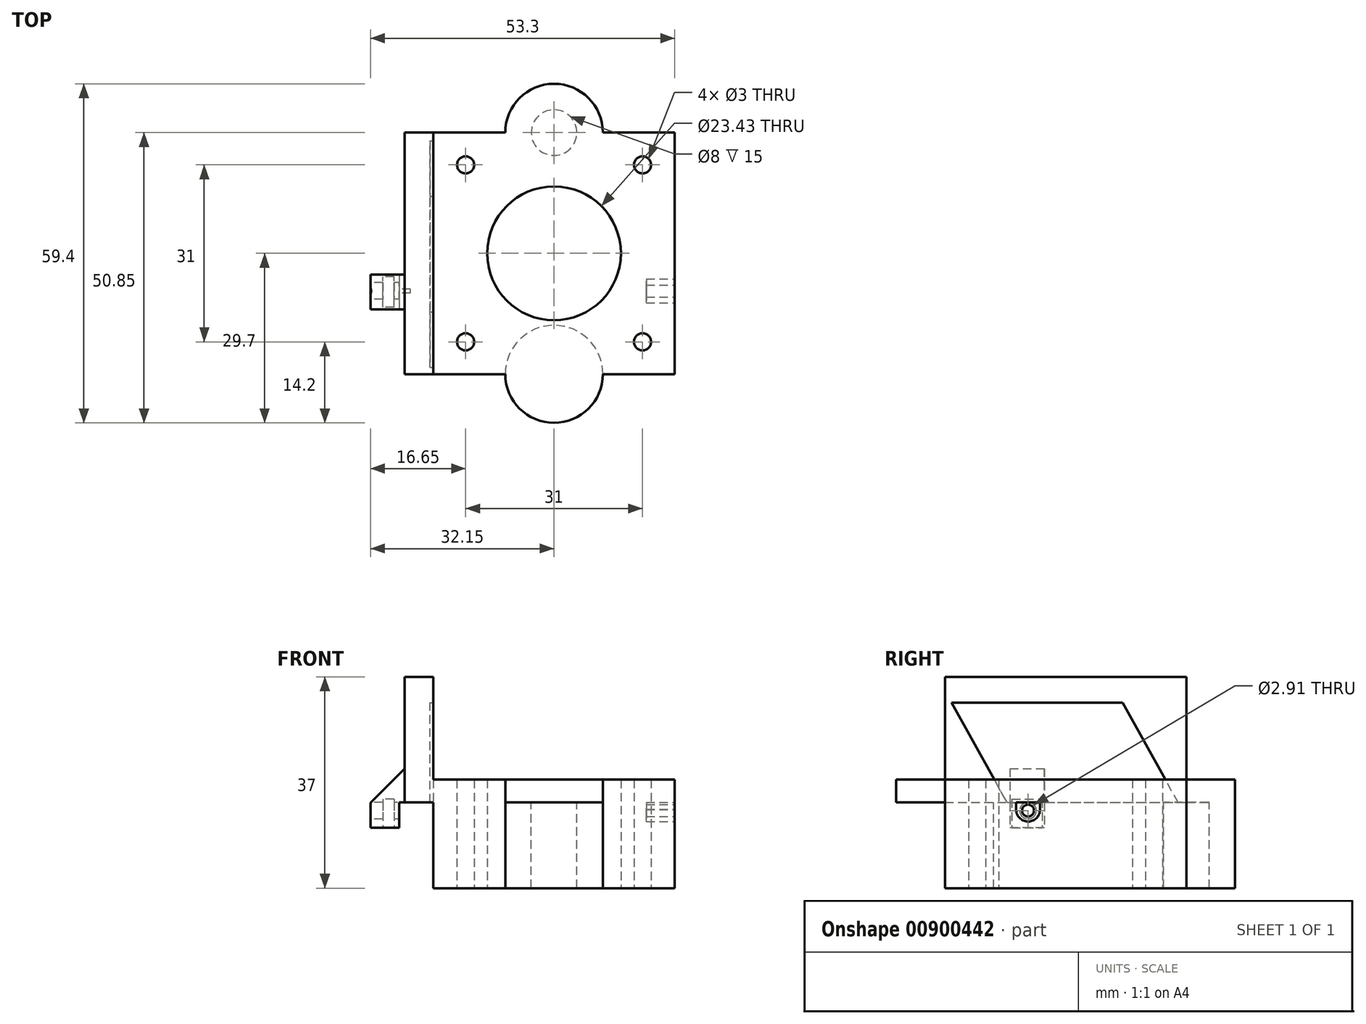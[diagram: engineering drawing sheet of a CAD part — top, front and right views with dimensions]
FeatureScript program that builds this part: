
annotation { "Feature Type Name" : "Feature", "Feature Type Description" : "" }
export const myFeature = defineFeature(function(context is Context, id is Id, definition is map)
    precondition{}
    {
        {
            var Q0;
            Q0=qCreatedBy(makeId("Top.planeOp"),FACE);
            var sketch = newSketch(context, id + "F0", { "sketchPlane" : qUnion([Q0])});
            skLineSegment(sketch, "E0.bottom", {"start": v(21.15, 21.15) * mm, "end": v(8.55, 21.15) * mm});
            skLineSegment(sketch, "E0.top", {"start": v(21.15, -21.15) * mm, "end": v(8.55, -21.15) * mm});
            skLineSegment(sketch, "E0.left", {"start": v(21.15, 21.15) * mm, "end": v(21.15, -21.15) * mm});
            skLineSegment(sketch, "E0.right", {"start": v(-21.15, 21.15) * mm, "end": v(-21.15, -21.15) * mm});
            skPoint(sketch, "E0.middle", {"position": v(0, 0) * mm});
            skCircle(sketch, "E1", {"center": v(-15.5, 15.5) * mm, "radius": 1.5 * mm});
            skCircle(sketch, "E2", {"center": v(15.5, 15.5) * mm, "radius": 1.5 * mm});
            skCircle(sketch, "E3", {"center": v(-15.5, -15.5) * mm, "radius": 1.5 * mm});
            skCircle(sketch, "E4", {"center": v(15.5, -15.5) * mm, "radius": 1.5 * mm});
            skCircle(sketch, "E5", {"center": v(0, 0) * mm, "radius": 11.71 * mm});
            skArc(sketch, "E6", {"start": v(0, 29.7) * mm, "mid": v(6.04, 27.2) * mm, "end": v(8.55, 21.15) * mm});
            skPoint(sketch, "E6.startSnap0", {"position": v(0, 21.15) * mm});
            skArc(sketch, "E7", {"start": v(0, 29.7) * mm, "mid": v(-6.04, 27.2) * mm, "end": v(-8.55, 21.15) * mm});
            skArc(sketch, "E8", {"start": v(-8.55, -21.15) * mm, "mid": v(0, -29.7) * mm, "end": v(8.55, -21.15) * mm});
            skLineSegment(sketch, "E9.trimOffspring", {"start": v(-8.55, -21.15) * mm, "end": v(-21.15, -21.15) * mm});
            skLineSegment(sketch, "E10.trimOffspring", {"start": v(-8.55, 21.15) * mm, "end": v(-21.15, 21.15) * mm});
            skSolve(sketch);
        }
        {
            var Q0;
            Q0=makeQuery(id+"F0.imprint","IMPRINT",FACE,{"disambiguationData":[TD([[makeQuery(id+"F0.imprint","IMPRINT",EDGE,{"derivedFrom":sQuery(id+"F0.wireOp",EDGE,"E0.bottom")}),1.0]])]});
            extrude(context, id + "F1", {"entities" : qUnion([Q0]), "depth" : 4 * mm, "offsetDistance" : 25 * mm});
        }
        {
            var Q0;
            Q0=makeQuery(id+"F1.opExtrude","CAP_FACE",FACE,{"disambiguationData":[OSD([sQuery(id+"F0.wireOp",EDGE,"E0.bottom"),sQuery(id+"F0.wireOp",EDGE,"E0.top"),sQuery(id+"F0.wireOp",EDGE,"E0.left"),sQuery(id+"F0.wireOp",EDGE,"E0.right"),sQuery(id+"F0.wireOp",EDGE,"E1"),sQuery(id+"F0.wireOp",EDGE,"E2"),sQuery(id+"F0.wireOp",EDGE,"E3"),sQuery(id+"F0.wireOp",EDGE,"E4"),sQuery(id+"F0.wireOp",EDGE,"E5"),sQuery(id+"F0.wireOp",EDGE,"E6"),sQuery(id+"F0.wireOp",EDGE,"E7"),sQuery(id+"F0.wireOp",EDGE,"E8"),sQuery(id+"F0.wireOp",EDGE,"E9.trimOffspring"),sQuery(id+"F0.wireOp",EDGE,"E10.trimOffspring")])],"isStart":true});
            var sketch = newSketch(context, id + "F2", { "sketchPlane" : qUnion([Q0])});
            skCircle(sketch, "E11", {"center": v(0, 21.15) * mm, "radius": 8.55 * mm});
            skCircle(sketch, "E12", {"center": v(0, 21.15) * mm, "radius": 4 * mm});
            skCircle(sketch, "E13", {"center": v(0, -21.15) * mm, "radius": 8.55 * mm});
            skCircle(sketch, "E14", {"center": v(0, -21.15) * mm, "radius": 4 * mm});
            skSolve(sketch);
        }
        {
            var Q0;
            Q0=makeQuery(id+"F2.imprint","IMPRINT",FACE,{"disambiguationData":[TD([[makeQuery(id+"F2.imprint","IMPRINT",EDGE,{"derivedFrom":sQuery(id+"F2.wireOp",EDGE,"E14")}),-1.0]])]});
            var Q1;
            {var subQ0=sQuery(id+"F2.wireOp",EDGE,"E11");Q1=makeQuery(id+"F2.imprint","IMPRINT",FACE,{"disambiguationData":[TD([[makeQuery(id+"F2.imprint","IMPRINT",EDGE,{"disambiguationData":[OD(0.0)],"derivedFrom":subQ0}),-1.0]])]});}
            extrude(context, id + "F3", {"entities" : qUnion([Q0, Q1]), "operationType" : NewBodyOperationType.ADD, "depth" : 15 * mm, "offsetDistance" : 25 * mm});
        }
        {
            var Q0;
            Q0=makeQuery(id+"F1.opExtrude","SWEPT_FACE",FACE,{"disambiguationData":[OSD([sQuery(id+"F0.wireOp",EDGE,"E0.right")])]});
            cPlane(context, id + "F4", {"entities" : qUnion([Q0]), "cplaneType" : CPlaneType.OFFSET, "offset" : 0 * mm, "width" : 150 * mm, "height" : 150 * mm});
        }
        {
            var Q0;
            Q0=qCreatedBy(id+"F4.planeOp",FACE);
            var sketch = newSketch(context, id + "F5", { "sketchPlane" : qUnion([Q0])});
            skLineSegment(sketch, "E15.bottom", {"start": v(-20, -0.53) * mm, "end": v(20, -0.53) * mm});
            skLineSegment(sketch, "E15.top", {"start": v(-20, 17.47) * mm, "end": v(20, 17.47) * mm});
            skLineSegment(sketch, "E15.left", {"start": v(-20, -0.53) * mm, "end": v(-20, 17.47) * mm});
            skLineSegment(sketch, "E15.right", {"start": v(20, -0.53) * mm, "end": v(20, 17.47) * mm});
            skPoint(sketch, "E15.middle", {"position": v(0, 8.47) * mm});
            skLineSegment(sketch, "E16", {"start": v(20, 17.47) * mm, "end": v(10, -0.53) * mm});
            skLineSegment(sketch, "E17", {"start": v(-20, -0.53) * mm, "end": v(-10, 17.47) * mm});
            skSolve(sketch);
        }
        {
            var Q0;
            {var subQ2=sQuery(id+"F5.wireOp",EDGE,"E16");Q0=makeQuery(id+"F5.imprint","IMPRINT",FACE,{"disambiguationData":[TD([[makeQuery(id+"F5.imprint","IMPRINT",EDGE,{"derivedFrom":subQ2}),-1.0]])]});}
            extrude(context, id + "F6", {"entities" : qUnion([Q0]), "depth" : 0.6 * mm, "offsetDistance" : 25 * mm});
        }
        {
            var Q0;
            Q0=makeQuery(id+"F1.opExtrude","SWEPT_FACE",FACE,{"disambiguationData":[OSD([sQuery(id+"F0.wireOp",EDGE,"E0.right")])]});
            var sketch = newSketch(context, id + "F7", { "sketchPlane" : qUnion([Q0])});
            skLineSegment(sketch, "E18.bottom", {"start": v(21.15, 0) * mm, "end": v(-21.15, 0) * mm});
            skLineSegment(sketch, "E18.top", {"start": v(21.15, 22) * mm, "end": v(-21.15, 22) * mm});
            skLineSegment(sketch, "E18.left", {"start": v(21.15, 0) * mm, "end": v(21.15, 22) * mm});
            skLineSegment(sketch, "E18.right", {"start": v(-21.15, 0) * mm, "end": v(-21.15, 22) * mm});
            skSolve(sketch);
        }
        {
            var Q0;
            Q0 = qSketchRegion(id + "F7", true);
            extrude(context, id + "F8", {"entities" : qUnion([Q0]), "depth" : 5 * mm, "offsetDistance" : 25 * mm});
        }
        {
            var Q0;
            Q0=makeQuery(id+"F8.opExtrude","SWEPT_BODY",BODY,{"disambiguationData":[OSD([sQuery(id+"F7.wireOp",EDGE,"E18.bottom"),sQuery(id+"F7.wireOp",EDGE,"E18.top"),sQuery(id+"F7.wireOp",EDGE,"E18.left"),sQuery(id+"F7.wireOp",EDGE,"E18.right")])]});
            var Q1;
            Q1=makeQuery(id+"F1.opExtrude","SWEPT_BODY",BODY,{"disambiguationData":[OSD([sQuery(id+"F0.wireOp",EDGE,"E0.bottom"),sQuery(id+"F0.wireOp",EDGE,"E0.top"),sQuery(id+"F0.wireOp",EDGE,"E0.left"),sQuery(id+"F0.wireOp",EDGE,"E0.right"),sQuery(id+"F0.wireOp",EDGE,"E1"),sQuery(id+"F0.wireOp",EDGE,"E2"),sQuery(id+"F0.wireOp",EDGE,"E3"),sQuery(id+"F0.wireOp",EDGE,"E4"),sQuery(id+"F0.wireOp",EDGE,"E5"),sQuery(id+"F0.wireOp",EDGE,"E6"),sQuery(id+"F0.wireOp",EDGE,"E7"),sQuery(id+"F0.wireOp",EDGE,"E8"),sQuery(id+"F0.wireOp",EDGE,"E9.trimOffspring"),sQuery(id+"F0.wireOp",EDGE,"E10.trimOffspring")])]});
            booleanBodies(context, id + "F9", {"operationType" : BooleanOperationType.UNION, "tools" : qUnion([Q0, Q1])});
        }
        {
            var Q0;
            Q0=makeQuery(id+"F6.opExtrude","SWEPT_BODY",BODY,{"disambiguationData":[OSD([sQuery(id+"F5.wireOp",EDGE,"E15.bottom"),sQuery(id+"F5.wireOp",EDGE,"E15.top"),sQuery(id+"F5.wireOp",EDGE,"E16"),sQuery(id+"F5.wireOp",EDGE,"E17")])]});
            var Q1;
            Q1=makeQuery(id+"F8.opExtrude","SWEPT_BODY",BODY,{"disambiguationData":[OSD([sQuery(id+"F7.wireOp",EDGE,"E18.bottom"),sQuery(id+"F7.wireOp",EDGE,"E18.top"),sQuery(id+"F7.wireOp",EDGE,"E18.left"),sQuery(id+"F7.wireOp",EDGE,"E18.right")])]});
            booleanBodies(context, id + "F10", {"operationType" : BooleanOperationType.SUBTRACTION, "tools" : qUnion([Q0]), "targets" : qUnion([Q1])});
        }
        {
            var Q0;
            Q0=makeQuery(id+"F1.opExtrude","SWEPT_FACE",FACE,{"disambiguationData":[OSD([sQuery(id+"F0.wireOp",EDGE,"E0.left")])]});
            var sketch = newSketch(context, id + "F11", { "sketchPlane" : qUnion([Q0])});
            skLineSegment(sketch, "E19.bottom", {"start": v(-4.5, 0) * mm, "end": v(-8.7, 0) * mm});
            skLineSegment(sketch, "E19.left", {"start": v(-4.5, 0) * mm, "end": v(-4.5, -1.2) * mm});
            skLineSegment(sketch, "E19.right", {"start": v(-8.7, 0) * mm, "end": v(-8.7, -1.26) * mm});
            skArc(sketch, "E20", {"start": v(-4.5, -1.2) * mm, "mid": v(-6.57, -3.33) * mm, "end": v(-8.7, -1.26) * mm});
            skCircle(sketch, "E21", {"center": v(-6.6, -1.42) * mm, "radius": 1.04 * mm});
            skSolve(sketch);
        }
        {
            var Q0;
            Q0=makeQuery(id+"F11.imprint","IMPRINT",FACE,{"disambiguationData":[TD([[makeQuery(id+"F11.imprint","IMPRINT",EDGE,{"derivedFrom":sQuery(id+"F11.wireOp",EDGE,"E19.bottom")}),1.0]])]});
            extrude(context, id + "F12", {"entities" : qUnion([Q0]), "oppositeDirection" : true, "depth" : 5 * mm, "offsetDistance" : 25 * mm});
        }
        {
            var Q0;
            Q0=makeQuery(id+"F12.opExtrude","CAP_FACE",FACE,{"disambiguationData":[OSD([sQuery(id+"F11.wireOp",EDGE,"E19.bottom"),sQuery(id+"F11.wireOp",EDGE,"E19.left"),sQuery(id+"F11.wireOp",EDGE,"E19.right"),sQuery(id+"F11.wireOp",EDGE,"E20"),sQuery(id+"F11.wireOp",EDGE,"E21")])],"isStart":false});
            cPlane(context, id + "F13", {"entities" : qUnion([Q0]), "cplaneType" : CPlaneType.OFFSET, "offset" : 33.4 * mm, "width" : 150 * mm, "height" : 150 * mm});
        }
        {
            var Q0;
            Q0=qCreatedBy(id+"F13.planeOp",FACE);
            var sketch = newSketch(context, id + "F14", { "sketchPlane" : qUnion([Q0])});
            skLineSegment(sketch, "E22.0.0", {"start": v(8.7, 0) * mm, "end": v(4.5, 0) * mm});
            skLineSegment(sketch, "E22.0.1", {"start": v(4.5, 0) * mm, "end": v(4.5, -1.2) * mm});
            skArc(sketch, "E22.0.2", {"start": v(4.5, -1.2) * mm, "mid": v(6.57, -3.33) * mm, "end": v(8.7, -1.26) * mm});
            skLineSegment(sketch, "E22.0.3", {"start": v(8.7, -1.26) * mm, "end": v(8.7, 0) * mm});
            skCircle(sketch, "E23.0", {"center": v(6.6, -1.42) * mm, "radius": 1.04 * mm});
            skSolve(sketch);
        }
        {
            var Q0;
            Q0 = qSketchRegion(id + "F14", true);
            extrude(context, id + "F15", {"entities" : qUnion([Q0]), "operationType" : NewBodyOperationType.ADD, "oppositeDirection" : true, "depth" : 5 * mm, "offsetDistance" : 25 * mm});
        }
        {
            var Q0;
            Q0=makeQuery(id+"F8.opExtrude","CAP_FACE",FACE,{"disambiguationData":[OSD([sQuery(id+"F7.wireOp",EDGE,"E18.bottom"),sQuery(id+"F7.wireOp",EDGE,"E18.top"),sQuery(id+"F7.wireOp",EDGE,"E18.left"),sQuery(id+"F7.wireOp",EDGE,"E18.right")])],"isStart":false});
            var sketch = newSketch(context, id + "F16", { "sketchPlane" : qUnion([Q0])});
            skCircle(sketch, "E24.0", {"center": v(6.6, -1.42) * mm, "radius": 1.04 * mm});
            skArc(sketch, "E25.0", {"start": v(4.5, -1.2) * mm, "mid": v(6.57, -3.33) * mm, "end": v(8.7, -1.26) * mm});
            skLineSegment(sketch, "E26.0.1", {"start": v(8.7, -1.26) * mm, "end": v(8.7, 0) * mm});
            skLineSegment(sketch, "E26.0.2", {"start": v(8.7, 0) * mm, "end": v(4.5, 0) * mm});
            skLineSegment(sketch, "E26.0.3", {"start": v(4.5, 0) * mm, "end": v(4.5, -1.2) * mm});
            skLineSegment(sketch, "E27.bottom", {"start": v(9.8, 5.94) * mm, "end": v(3.74, 5.94) * mm});
            skLineSegment(sketch, "E27.top", {"start": v(9.8, -4.4) * mm, "end": v(3.74, -4.4) * mm});
            skLineSegment(sketch, "E27.left", {"start": v(9.8, 5.94) * mm, "end": v(9.8, -4.4) * mm});
            skLineSegment(sketch, "E27.right", {"start": v(3.74, 5.94) * mm, "end": v(3.74, -4.4) * mm});
            skSolve(sketch);
        }
        {
            var Q0;
            Q0 = qSketchRegion(id + "F16", true);
            var Q1;
            Q1=makeQuery(id+"F16.imprint","IMPRINT",FACE,{"disambiguationData":[TD([[makeQuery(id+"F16.imprint","IMPRINT",EDGE,{"derivedFrom":sQuery(id+"F16.wireOp",EDGE,"E25.0")}),-1.0]])]});
            var Q2;
            Q2=makeQuery(id+"F16.imprint","IMPRINT",FACE,{"disambiguationData":[TD([[makeQuery(id+"F16.imprint","IMPRINT",EDGE,{"derivedFrom":sQuery(id+"F16.wireOp",EDGE,"E24.0")}),-1.0]])]});
            extrude(context, id + "F17", {"entities" : qUnion([Q0, Q1, Q2]), "operationType" : NewBodyOperationType.ADD, "depth" : 6 * mm, "offsetDistance" : 25 * mm});
        }
        {
            var Q0;
            Q0=makeQuery(id+"F17.opExtrude","CAP_EDGE",EDGE,{"disambiguationData":[OSD([sQuery(id+"F16.wireOp",EDGE,"E27.bottom")])],"isStart":false});
            chamfer(context, id + "F18", {"entities" : qUnion([Q0]), "width" : 6 * mm, "tangentPropagation" : true});
        }
        {
            var Q0;
            Q0=makeQuery(id+"F17.opExtrude","CAP_FACE",FACE,{"disambiguationData":[OSD([sQuery(id+"F16.wireOp",EDGE,"E24.0"),sQuery(id+"F16.wireOp",EDGE,"E27.bottom"),sQuery(id+"F16.wireOp",EDGE,"E27.top"),sQuery(id+"F16.wireOp",EDGE,"E27.left"),sQuery(id+"F16.wireOp",EDGE,"E27.right")])],"isStart":false});
            var sketch = newSketch(context, id + "F19", { "sketchPlane" : qUnion([Q0])});
            skCircle(sketch, "E28", {"center": v(6.6, -1.42) * mm, "radius": 1.46 * mm});
            skSolve(sketch);
        }
        {
            var Q0;
            Q0 = qSketchRegion(id + "F19", true);
            extrude(context, id + "F20", {"entities" : qUnion([Q0]), "operationType" : NewBodyOperationType.REMOVE, "oppositeDirection" : true, "depth" : 7 * mm, "offsetDistance" : 25 * mm});
        }
        {
            var Q0;
            Q0=makeQuery(id+"F17.opExtrude","SWEPT_FACE",FACE,{"disambiguationData":[OSD([sQuery(id+"F16.wireOp",EDGE,"E27.top")])]});
            var sketch = newSketch(context, id + "F21", { "sketchPlane" : qUnion([Q0])});
            skLineSegment(sketch, "E29.bottom", {"start": v(-28.03, 9.43) * mm, "end": v(-30.02, 9.43) * mm});
            skLineSegment(sketch, "E29.top", {"start": v(-28.03, 4.1) * mm, "end": v(-30.02, 4.1) * mm});
            skLineSegment(sketch, "E29.left", {"start": v(-28.03, 9.43) * mm, "end": v(-28.03, 4.1) * mm});
            skLineSegment(sketch, "E29.right", {"start": v(-30.02, 9.43) * mm, "end": v(-30.02, 4.1) * mm});
            skSolve(sketch);
        }
        {
            var Q0;
            Q0=makeQuery(id+"F21.imprint","IMPRINT",FACE,{"disambiguationData":[TD([[makeQuery(id+"F21.imprint","IMPRINT",EDGE,{"derivedFrom":sQuery(id+"F21.wireOp",EDGE,"E29.bottom")}),1.0]])]});
            extrude(context, id + "F22", {"entities" : qUnion([Q0]), "operationType" : NewBodyOperationType.REMOVE, "oppositeDirection" : true, "depth" : 5 * mm, "offsetDistance" : 25 * mm});
        }
        {
            var Q0;
            Q0=makeQuery(id+"F17.opExtrude","CAP_FACE",FACE,{"disambiguationData":[OSD([sQuery(id+"F16.wireOp",EDGE,"E24.0"),sQuery(id+"F16.wireOp",EDGE,"E27.bottom"),sQuery(id+"F16.wireOp",EDGE,"E27.top"),sQuery(id+"F16.wireOp",EDGE,"E27.left"),sQuery(id+"F16.wireOp",EDGE,"E27.right")])],"isStart":true});
            var sketch = newSketch(context, id + "F23", { "sketchPlane" : qUnion([Q0])});
            skLineSegment(sketch, "E30.bottom", {"start": v(-3.74, 0) * mm, "end": v(-9.8, 0) * mm});
            skLineSegment(sketch, "E30.top", {"start": v(-3.74, -5.25) * mm, "end": v(-9.8, -5.25) * mm});
            skLineSegment(sketch, "E30.left", {"start": v(-3.74, 0) * mm, "end": v(-3.74, -5.25) * mm});
            skLineSegment(sketch, "E30.right", {"start": v(-9.8, 0) * mm, "end": v(-9.8, -5.25) * mm});
            skSolve(sketch);
        }
        {
            var Q0;
            Q0 = qSketchRegion(id + "F23", true);
            extrude(context, id + "F24", {"entities" : qUnion([Q0]), "operationType" : NewBodyOperationType.REMOVE, "oppositeDirection" : true, "depth" : 1 * mm, "offsetDistance" : 25 * mm});
        }
    });
